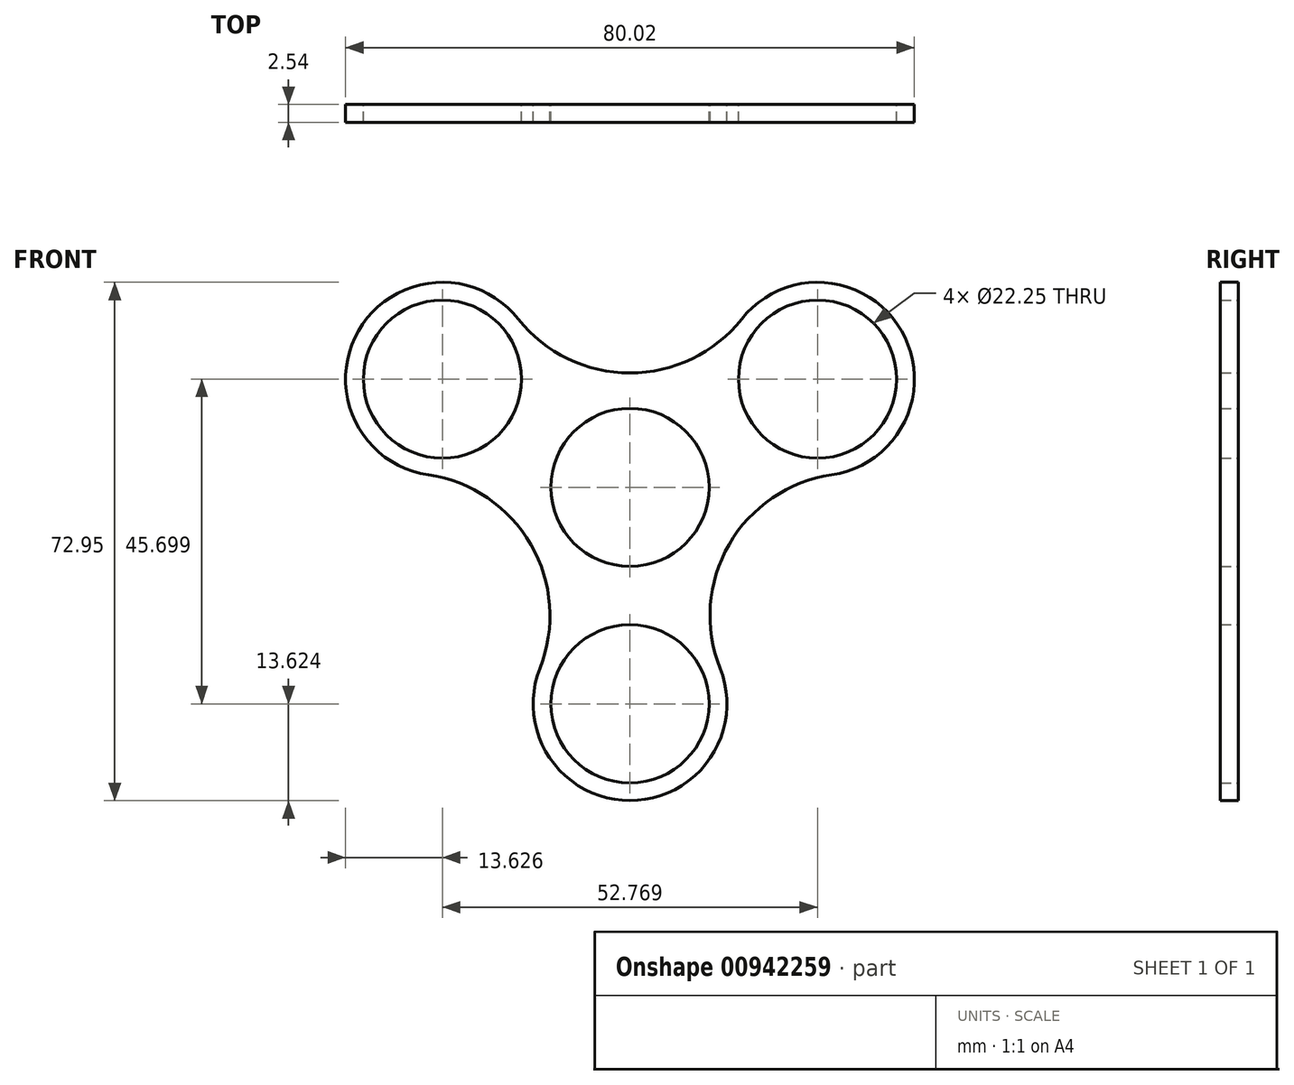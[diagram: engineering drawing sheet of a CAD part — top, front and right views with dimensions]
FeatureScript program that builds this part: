
annotation { "Feature Type Name" : "Feature", "Feature Type Description" : "" }
export const myFeature = defineFeature(function(context is Context, id is Id, definition is map)
    precondition{}
    {
        {
            var Q0;
            Q0=qCreatedBy(makeId("Front.planeOp"),FACE);
            var sketch = newSketch(context, id + "F0", { "sketchPlane" : qUnion([Q0])});
            skCircle(sketch, "E0", {"center": v(0, 0) * mm, "radius": 11.12 * mm});
            skCircle(sketch, "E1", {"center": v(0, -30.47) * mm, "radius": 11.12 * mm});
            skCircle(sketch, "E2.1.0", {"center": v(26.38, 15.23) * mm, "radius": 11.12 * mm});
            skCircle(sketch, "E2.2.0", {"center": v(-26.38, 15.23) * mm, "radius": 11.12 * mm});
            skCircle(sketch, "E3.0", {"center": v(26.38, 15.23) * mm, "radius": 13.62 * mm});
            skCircle(sketch, "E4.0", {"center": v(0, -30.47) * mm, "radius": 13.62 * mm});
            skCircle(sketch, "E5.0", {"center": v(-26.38, 15.23) * mm, "radius": 13.62 * mm});
            skCircle(sketch, "E6", {"center": v(-31.28, -18.06) * mm, "radius": 20.03 * mm});
            skCircle(sketch, "E7.1.0", {"center": v(31.28, -18.06) * mm, "radius": 20.03 * mm});
            skCircle(sketch, "E7.2.0", {"center": v(0, 36.12) * mm, "radius": 20.03 * mm});
            skSolve(sketch);
        }
        {
            var Q0;
            Q0=makeQuery(id+"F0.imprint","IMPRINT",FACE,{"disambiguationData":[TD([[makeQuery(id+"F0.imprint","IMPRINT",EDGE,{"derivedFrom":sQuery(id+"F0.wireOp",EDGE,"E0")}),-1.0]])]});
            var Q1;
            Q1=makeQuery(id+"F0.imprint","IMPRINT",FACE,{"disambiguationData":[TD([[makeQuery(id+"F0.imprint","IMPRINT",EDGE,{"derivedFrom":sQuery(id+"F0.wireOp",EDGE,"E2.2.0")}),-1.0]])]});
            var Q2;
            Q2=makeQuery(id+"F0.imprint","IMPRINT",FACE,{"disambiguationData":[TD([[makeQuery(id+"F0.imprint","IMPRINT",EDGE,{"derivedFrom":sQuery(id+"F0.wireOp",EDGE,"E2.1.0")}),-1.0]])]});
            var Q3;
            Q3=makeQuery(id+"F0.imprint","IMPRINT",FACE,{"disambiguationData":[TD([[makeQuery(id+"F0.imprint","IMPRINT",EDGE,{"derivedFrom":sQuery(id+"F0.wireOp",EDGE,"E1")}),-1.0]])]});
            extrude(context, id + "F1", {"entities" : qUnion([Q0, Q1, Q2, Q3]), "depth" : 2.54 * mm, "offsetDistance" : 25.4 * mm});
        }
    });
